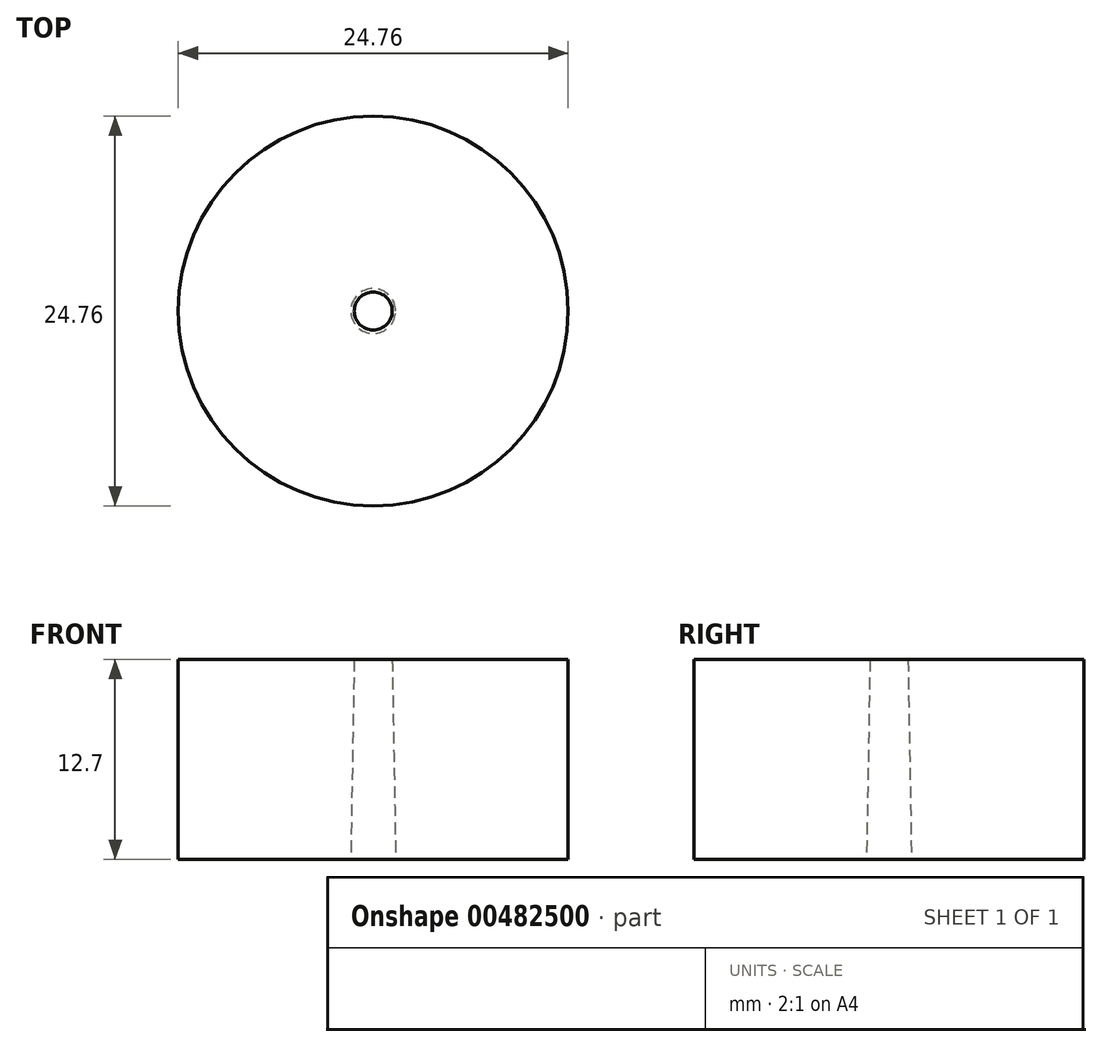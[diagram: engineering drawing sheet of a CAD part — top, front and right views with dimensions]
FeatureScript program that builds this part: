
annotation { "Feature Type Name" : "Feature", "Feature Type Description" : "" }
export const myFeature = defineFeature(function(context is Context, id is Id, definition is map)
    precondition{}
    {
        {
            var Q0;
            Q0=qCreatedBy(makeId("Top.planeOp"),FACE);
            var sketch = newSketch(context, id + "F0", { "sketchPlane" : qUnion([Q0])});
            skCircle(sketch, "E0", {"center": v(0, 0) * mm, "radius": 12.38 * mm});
            skSolve(sketch);
        }
        {
            var Q0;
            Q0=makeQuery(id+"F0.imprint","IMPRINT",FACE,{"disambiguationData":[TD([[makeQuery(id+"F0.imprint","IMPRINT",EDGE,{"derivedFrom":sQuery(id+"F0.wireOp",EDGE,"E0")}),1.0]])]});
            extrude(context, id + "F1", {"entities" : qUnion([Q0]), "depth" : 12.7 * mm});
        }
        {
            var Q0;
            Q0=makeQuery(id+"F1.opExtrude","CAP_FACE",FACE,{"disambiguationData":[OSD([sQuery(id+"F0.wireOp",EDGE,"E0")])],"isStart":false});
            var sketch = newSketch(context, id + "F2", { "sketchPlane" : qUnion([Q0])});
            skCircle(sketch, "E1", {"center": v(0, 0) * mm, "radius": 1.2 * mm});
            skSolve(sketch);
        }
        {
            var Q0;
            Q0=makeQuery(id+"F2.imprint","IMPRINT",FACE,{"disambiguationData":[TD([[makeQuery(id+"F2.imprint","IMPRINT",EDGE,{"derivedFrom":sQuery(id+"F2.wireOp",EDGE,"E1")}),1.0]])]});
            extrude(context, id + "F3", {"entities" : qUnion([Q0]), "operationType" : NewBodyOperationType.REMOVE, "oppositeDirection" : true, "depth" : 25.4 * mm, "hasDraft" : true, "draftAngle" : 1 * degree});
        }
    });
